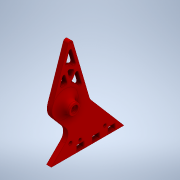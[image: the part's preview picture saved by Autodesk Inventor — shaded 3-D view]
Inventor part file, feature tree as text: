
AUTODESK INVENTOR PART (.ipt)
format: ipt  version: 2020 (Build 240168000, 168)  size: 322,048 bytes
history: native  units: mm
features: extrude x7, sketch x7, other x3, fillet x1, chamfer x1, projected_geometry x1
ambient origin geometry x8: Origin, YZ Plane, XZ Plane, XY Plane, X Axis, Y Axis, Z Axis, Center Point
bodies: Solid1 (feature_tree)
feature tree (20):
  other  "WeaponMountBasePlateV1.ipt"
  extrude  "Extrusion1"  Depth=10.0mm
  extrude  "Extrusion2"  TaperAngle=0.0deg  [1 undecoded]
  extrude  "Extrusion3"  Depth=0.75mm
  fillet  "Fillet2"  [1 undecoded]
  extrude  "Extrusion4"  Depth=1.9mm
  extrude  "Extrusion5"  Depth=8.0mm
  extrude  "Extrusion6"  Depth=10.0mm TaperAngle=0.0deg
  chamfer  "Chamfer1"  [1 undecoded]
  extrude  "Extrusion7"  Depth=2.0mm
  other  "Solid1::WeaponMountBasePlateV1.ipt"
  other  "TaggingFeature1"
  sketch  "Sketch2"  dims[d0=10.0mm d2=11.3mm]
  sketch  "Sketch3"  dims[d3=10.0mm d4=0.0mm]
  sketch  "Sketch4"  dims[d5=7.3mm d6=0.75mm d7=0.0mm]
  projected_geometry  "Projected Loop1"
  sketch  "Sketch5"  dims[d8=7.3mm d9=1.9mm]
  sketch  "Sketch6"  dims[d10=0.0mm d12=8.0mm]
  sketch  "Sketch7"  dims[d13=4.5mm d14=10.0mm d15=0.0mm]
  sketch  "Sketch8"  dims[d16=2.2mm d17=0.0mm d18=0.0mm d19=4.0mm d20=2.0mm d21=0.0mm d22=0.9mm d23=2.0mm d24=45.0deg d25=6.1mm d26=0.0mm d27=-7.853982mm]
note: 3 required parameter values undecoded (feature->parameter linkage not recoverable at this tier; creation-order binding heuristic only, values carry confidence <= 0.55)
